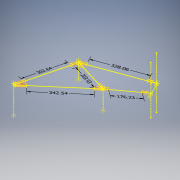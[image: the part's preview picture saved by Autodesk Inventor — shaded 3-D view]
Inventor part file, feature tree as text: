
AUTODESK INVENTOR PART (.ipt)
format: ipt  version: 2018 (Build 220112000, 112)  size: 508,928 bytes
history: native  units: mm
features: other x21, plane x18, sketch x10, surface_op x10, split x8, delete_face x7, extrude x5, boolean_combine x1
ambient origin geometry x8: Origin, YZ Plane, XZ Plane, XY Plane, X Axis, Y Axis, Z Axis, Center Point
bodies: Solid4 (feature_tree), Solid5 (feature_tree), Solid6 (feature_tree), Solid7 (feature_tree), Solid8 (feature_tree), Solid1 (feature_tree), Solid2 (feature_tree), Solid9 (feature_tree)
feature tree (80):
  other  "MainFrame.ipt"
  other  "Annotations"
  extrude  "Extrusion1"  Depth=10.0mm TaperAngle=0.0deg
  extrude  "Extrusion2"  [1 undecoded]
  extrude  "Extrusion3"  Depth=62.0mm TaperAngle=0.0deg
  plane  "Work Plane8"
  extrude  "Extrusion4"  Depth=46.5mm TaperAngle=0.0deg
  plane  "Work Plane9"
  extrude  "Extrusion5"  Depth=45.25mm
  boolean_combine  "Combine1"
  plane  "Work Plane10"
  plane  "Work Plane12"
  plane  "Work Plane14"
  plane  "Work Plane5"
  plane  "Work Plane7"
  plane  "Work Plane15"
  split  "Split4"
  split  "Split5"
  split  "Split6"
  split  "Split7"
  split  "Split8"
  plane  "Work Plane17"
  split  "Split9"
  delete_face  "Delete Face7"
  plane  "Work Plane19"
  split  "Split10"
  plane  "Work Plane21"
  split  "Split11"
  delete_face  "Delete Face8"
  delete_face  "Delete Face9"
  delete_face  "Delete Face10"
  delete_face  "Delete Face11"
  delete_face  "Delete Face12"
  delete_face  "Delete Face13"
  sketch  "Sketch6"  dims[d16=27.75mm]
  surface_op  "Trim1"
  surface_op  "Trim11"
  sketch  "Sketch7"  dims[d17=47.5mm]
  surface_op  "Trim3"
  surface_op  "Trim4"
  sketch  "Sketch8"  dims[d18=40.25mm]
  surface_op  "Trim5"
  surface_op  "Trim6"
  sketch  "Sketch9"  dims[d19=-43.0mm]
  surface_op  "Trim7"
  surface_op  "Trim12"
  sketch  "Sketch10"  dims[d20=0.0mm d21=0.0mm d22=0.0mm d23=0.0mm d24=0.0mm d25=0.0mm d26=0.0mm d27=0.0mm d28=0.0mm d29=0.0mm d30=0.0mm d31=0.0mm d32=0.0mm d33=0.0mm d36=0.0mm d37=0.0mm d40=1.0mm d41=8.0mm d42=1.0mm d44=8.0mm d45=1.0mm d46=8.0mm d47=1.0mm d48=8.0mm d49=1.0mm d56=0.0mm d57=0.0mm d58=0.0mm d59=0.0mm d51=342.54257mm d52=203.925865mm d55=176.233459mm d60=328.06463mm d61=302.640454mm]
  surface_op  "Trim9"
  surface_op  "Trim10"
  other  "Frame::MainFrame.ipt"
  other  "PivotPlateRight::MainFrame.ipt"
  other  "TaggingFeature1"
  sketch  "Sketch1"  dims[d0=10.0mm d1=92.0mm d2=0.0mm]
  sketch  "Sketch2"  dims[d3=46.5mm d4=0.0mm d6=-65.75mm]
  plane  "Work Plane4"
  plane  "Work Plane6"
  sketch  "Sketch3"  dims[d7=-69.5mm d8=62.0mm d9=0.0mm]
  sketch  "Sketch4"  dims[d10=46.5mm d11=0.0mm d12=46.5mm d13=0.0mm]
  sketch  "Sketch5"  dims[d14=-38.5mm d15=45.25mm]
  plane  "Work Plane11"
  plane  "Work Plane13"
  plane  "Work Plane16"
  plane  "Work Plane18"
  plane  "Work Plane20"
  other  "HeadTube::MainFrame.ipt"
  other  "OffsetSrf1"
  other  "OffsetSrf2"
  other  "OffsetSrf3"
  other  "OffsetSrf4"
  other  "OffsetSrf5"
  other  "OffsetSrf6"
  other  "OffsetSrf7"
  other  "OffsetSrf9"
  other  "OffsetSrf11"
  other  "OffsetSrf12"
  other  "Linear Dimension 2"
  other  "Linear Dimension 3"
  other  "Linear Dimension 5"
  other  "Linear Dimension 6"
  other  "Linear Dimension 7"
note: 1 required parameter value undecoded (feature->parameter linkage not recoverable at this tier; creation-order binding heuristic only, values carry confidence <= 0.55)
